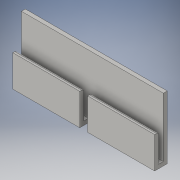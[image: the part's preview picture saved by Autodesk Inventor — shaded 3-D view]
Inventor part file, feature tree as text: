
AUTODESK INVENTOR PART (.ipt)
format: ipt  version: 2016 (Build 200138000, 138)  size: 153,600 bytes
history: native  units: in
note: dims shown in document units (in); Inventor stores cm internally (conversion verified against a paired STEP export)
features: extrude x4, sketch x4, projected_geometry x4
ambient origin geometry x8: Origin, YZ Plane, XZ Plane, XY Plane, X Axis, Y Axis, Z Axis, Center Point
bodies: Body1 (feature_tree)
feature tree (12):
  extrude  "Extrusion4"  Depth=0.8in
  extrude  "Extrusion5"  Depth=0.3in
  extrude  "Extrusion6"  Depth=2.0in
  extrude  "Extrusion7"  Depth=0.3in
  sketch  "Sketch5"  dims[d26=4.0in d27=0.8in]
  sketch  "Sketch6"  dims[d28=3.75in d29=0.3in]
  sketch  "Sketch7"  dims[d30=0.25in d31=2.0in]
  projected_geometry  "Projected Loop2"
  sketch  "Sketch8"  dims[d32=9.0in d33=0.0in d34=0.3in d35=3.75in d36=0.25in d37=2.0in d38=9.0in d39=0.0in d40=2.0in d41=9.0in d42=0.0in d43=0.5in d44=4.25in d45=9.0in d46=0.0in d47=0.125in d48=0.125in]
  projected_geometry  "Projected Loop3"
  projected_geometry  "Projected Loop4"
  projected_geometry  "Projected Loop5"
